# Revit family: NBS_DuPontCorian_ShowerTrays_Smart
name_source: partatom
category: Plumbing Fixtures
revit_build: Autodesk Revit 2015 (Build: 20140223_1515(x64)
units: mm (PartAtom-declared; Revit-internal decimal feet)

## types (12) — shared parameters
AssetType = Fixed
Color = Glacier white
Depth = 30 mm  [stored 0.0984252 ft]
DrainSize = 90 mm
DurationUnit = year
HasTray = Yes
IfcExportAs = IfcSanitaryTerminalType
IfcExportType = SHOWER
ManufacturerName = DuPont™ Corian®
ManufacturerURL = www.corian.co.uk
NBSCertification = www.nationalbimlibrary.com/cert/4p2cz4hj
NBSDescription = Shower trays
NBSReference = 45-35-70/336
NominalHeight = 30 mm  [stored 0.0984252 ft]
ProductInformation = www.dupont.co.uk/products-and-services/construction-materials/surface-design-materials/brands/corian-solid-surfaces/products/sinks.html?elqTrackId=01f5f20e93e848a3ab5f9e2efde4dc0f&elqaid=1733&elqat=2
Shape = Rectangular
ShowerTrayMaterial = NBS_Concept
ShowerType = NotKnown
TrayPlacementAboveSurface = 1 mm  [stored 0.00328084 ft]
Uniclass2015Code = Pr_40_20_06_84
Uniclass2015Title = Shower trays
Uniclass2015Version = Products v1.3
Version = 1
WarrantyDurationUnit = year
zero-valued in all types: Default Elevation, MaterialThickness, NominalWidth, WFU

## per-type parameters (varying)
| type | BIMObjectName | Length | ModelNumber | ModelReference | Name | NominalDepth | NominalLength | Size | SlopeLength | SlopeWidth | Width |
| Smart_8211 | NBS_DuPontCorian_ShowerTrays_Smart_8211 | 1200 mm | 8211 | Smart 8211 | ShowerTrays_Smart8211_DuPont Corian | 800 mm  [stored 2.62467 ft] | 1200 mm | 1200x800x30mm | 700 mm  [stored 2.29659 ft] | 700 mm  [stored 2.29659 ft] | 800 mm  [stored 2.62467 ft] |
| Smart_8212 | NBS_DuPontCorian_ShowerTrays_Smart_8212 | 1200 mm | 8212 | Smart 8212 | ShowerTrays_Smart8212_DuPont Corian | 800 mm  [stored 2.62467 ft] | 1200 mm | 1200x800x30mm | 1100 mm | 700 mm  [stored 2.29659 ft] | 800 mm  [stored 2.62467 ft] |
| Smart_8213 | NBS_DuPontCorian_ShowerTrays_Smart_8213 | 1400 mm | 8213 | Smart 8213 | ShowerTrays_Smart8213_DuPont Corian | 800 mm  [stored 2.62467 ft] | 1400 mm | 1400x800x30mm | 1100 mm | 700 mm  [stored 2.29659 ft] | 800 mm  [stored 2.62467 ft] |
| Smart_8214 | NBS_DuPontCorian_ShowerTrays_Smart_8214 | 1600 mm | 8214 | Smart 8214 | ShowerTrays_Smart8214_DuPont Corian | 800 mm  [stored 2.62467 ft] | 1600 mm | 1600x800x30mm | 1100 mm | 700 mm  [stored 2.29659 ft] | 800 mm  [stored 2.62467 ft] |
| Smart_8215 | NBS_DuPontCorian_ShowerTrays_Smart_8215 | 1800 mm | 8215 | Smart 8215 | ShowerTrays_Smart8215_DuPont Corian | 800 mm  [stored 2.62467 ft] | 1800 mm | 1800x800x30mm | 1100 mm | 700 mm  [stored 2.29659 ft] | 800 mm  [stored 2.62467 ft] |
| Smart_8216 | NBS_DuPontCorian_ShowerTrays_Smart_8216 | 2000 mm | 8216 | Smart 8216 | ShowerTrays_Smart8216_DuPont Corian | 800 mm  [stored 2.62467 ft] | 2000 mm | 2000x800x30mm | 1100 mm | 700 mm  [stored 2.29659 ft] | 800 mm  [stored 2.62467 ft] |
| Smart_8221 | NBS_DuPontCorian_ShowerTrays_Smart_8221 | 1200 mm | 8221 | Smart 8221 | ShowerTrays_Smart8221_DuPont Corian | 900 mm | 1200 mm | 1200x900x30mm | 800 mm  [stored 2.62467 ft] | 800 mm  [stored 2.62467 ft] | 900 mm |
| Smart_8222 | NBS_DuPontCorian_ShowerTrays_Smart_8222 | 1200 mm | 8222 | Smart 8222 | ShowerTrays_Smart8222_DuPont Corian | 900 mm | 1200 mm | 1200x900x30mm | 1100 mm | 800 mm  [stored 2.62467 ft] | 900 mm |
| Smart_8223 | NBS_DuPontCorian_ShowerTrays_Smart_8223 | 1400 mm | 8223 | Smart 8223 | ShowerTrays_Smart8223_DuPont Corian | 900 mm | 1400 mm | 1400x900x30mm | 1100 mm | 800 mm  [stored 2.62467 ft] | 900 mm |
| Smart_8224 | NBS_DuPontCorian_ShowerTrays_Smart_8224 | 1600 mm | 8224 | Smart 8224 | ShowerTrays_Smart8224_DuPont Corian | 900 mm | 1600 mm | 1600x900x30mm | 1100 mm | 800 mm  [stored 2.62467 ft] | 900 mm |
| Smart_8225 | NBS_DuPontCorian_ShowerTrays_Smart_8225 | 1800 mm | 8225 | Smart 8225 | ShowerTrays_Smart8225_DuPont Corian | 900 mm | 1800 mm | 1800x900x30mm | 1100 mm | 800 mm  [stored 2.62467 ft] | 900 mm |
| Smart_8226 | NBS_DuPontCorian_ShowerTrays_Smart_8226 | 2000 mm | 8226 | Smart 8226 | ShowerTrays_Smart8226_DuPont Corian | 900 mm | 2000 mm | 2000x900x30mm | 1100 mm | 800 mm  [stored 2.62467 ft] | 900 mm |

note: [stored X ft] marks values corroborated as IEEE doubles in the binary element streams (Revit-internal decimal feet)

## geometry (parser evidence)
native form markers: Sweep x2
no freeform markers — native parametric forms only
